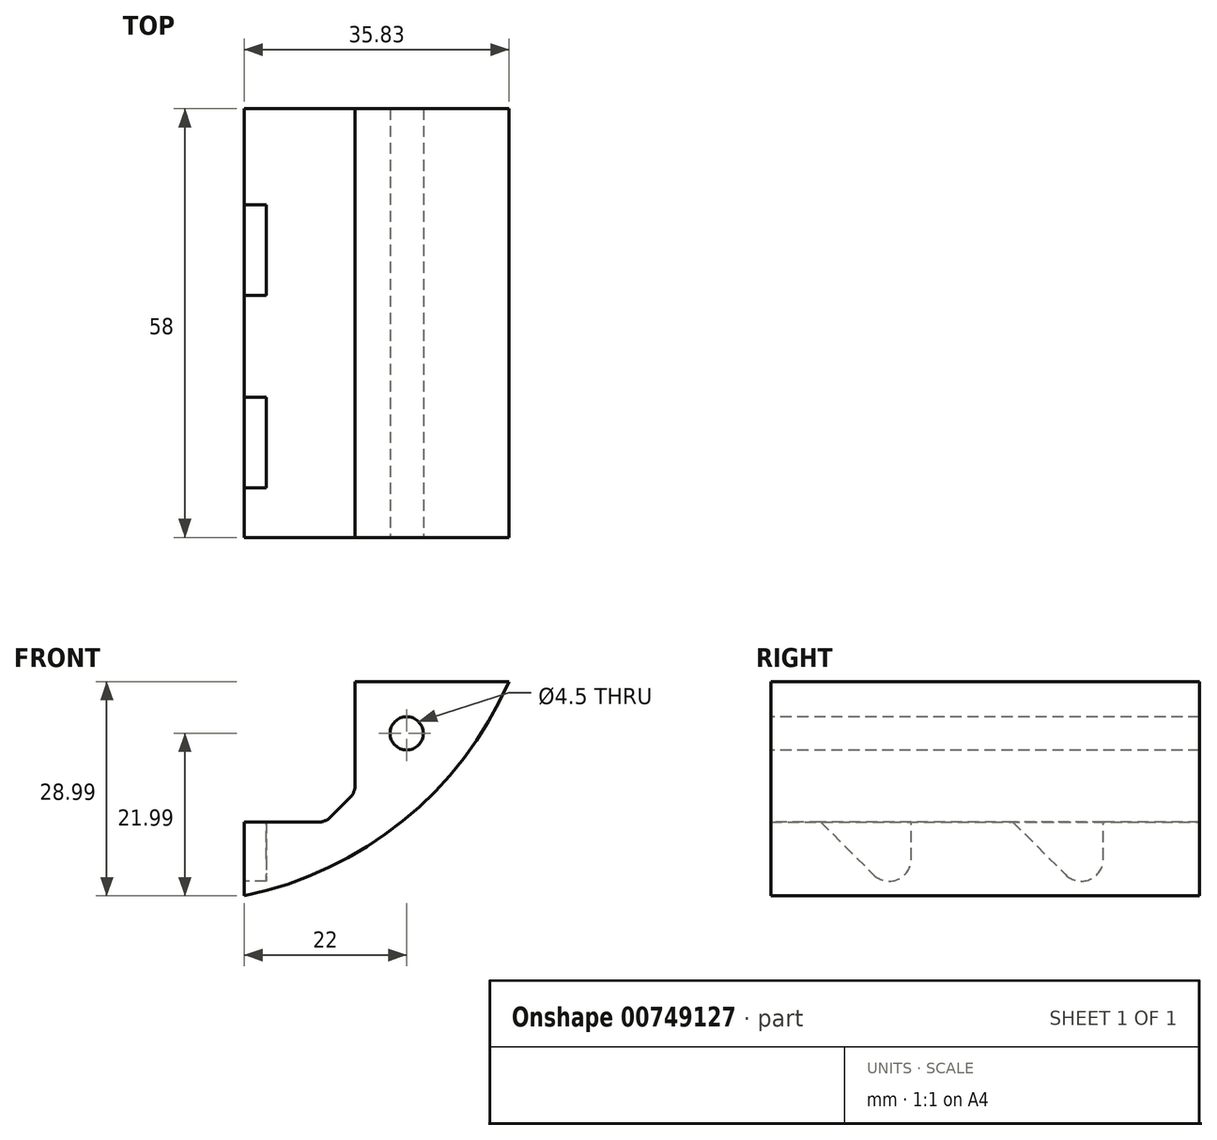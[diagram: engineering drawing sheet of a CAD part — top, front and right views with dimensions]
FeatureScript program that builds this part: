
annotation { "Feature Type Name" : "Feature", "Feature Type Description" : "" }
export const myFeature = defineFeature(function(context is Context, id is Id, definition is map)
    precondition{}
    {
        {
            var Q0;
            Q0=qCreatedBy(makeId("Front.planeOp"),FACE);
            var sketch = newSketch(context, id + "F0", { "sketchPlane" : qUnion([Q0])});
            skArc(sketch, "E0", {"start": v(10, -48.99) * mm, "mid": v(31.45, -38.87) * mm, "end": v(45.83, -20) * mm});
            skLineSegment(sketch, "E1", {"start": v(45.83, -20) * mm, "end": v(10, -20) * mm});
            skLineSegment(sketch, "E2", {"start": v(10, -20) * mm, "end": v(10, -48.99) * mm});
            skSolve(sketch);
        }
        {
            var Q0;
            Q0 = qSketchRegion(id + "F0", true);
            extrude(context, id + "F1", {"entities" : qUnion([Q0]), "endBound" : BoundingType.SYMMETRIC, "depth" : 58 * mm, "offsetDistance" : 25 * mm});
        }
        {
            var Q0;
            Q0=makeQuery(id+"F1.opExtrude","CAP_FACE",FACE,{"disambiguationData":[OSD([sQuery(id+"F0.wireOp",EDGE,"E0"),sQuery(id+"F0.wireOp",EDGE,"E1"),sQuery(id+"F0.wireOp",EDGE,"E2")])],"isStart":false});
            var sketch = newSketch(context, id + "F2", { "sketchPlane" : qUnion([Q0])});
            skLineSegment(sketch, "E3.bottom", {"start": v(10, -20) * mm, "end": v(25, -20) * mm});
            skLineSegment(sketch, "E3.top", {"start": v(10, -38.99) * mm, "end": v(25, -38.99) * mm});
            skLineSegment(sketch, "E3.left", {"start": v(10, -20) * mm, "end": v(10, -38.99) * mm});
            skLineSegment(sketch, "E3.right", {"start": v(25, -20) * mm, "end": v(25, -38.99) * mm});
            skSolve(sketch);
        }
        {
            var Q0;
            Q0 = qSketchRegion(id + "F2", true);
            extrude(context, id + "F3", {"entities" : qUnion([Q0]), "operationType" : NewBodyOperationType.REMOVE, "endBound" : BoundingType.THROUGH_ALL, "oppositeDirection" : true, "depth" : 25 * mm, "offsetDistance" : 25 * mm});
        }
        {
            var Q0;
            Q0=makeQuery(id+"F3.boolean.opBoolean","COPY",EDGE,{"derivedFrom":makeQuery(id+"F3.opExtrude","SWEPT_EDGE",EDGE,{"disambiguationData":[OSD([sQuery(id+"F2.wireOp",EDGE,"E3.top"),sQuery(id+"F2.wireOp",EDGE,"E3.right")])]})});
            chamfer(context, id + "F4", {"entities" : qUnion([Q0]), "width" : 4 * mm, "tangentPropagation" : true});
        }
        {
            var Q0;
            Q0=makeQuery(id+"F1.opExtrude","SWEPT_FACE",FACE,{"disambiguationData":[OSD([sQuery(id+"F0.wireOp",EDGE,"E2")])]});
            var sketch = newSketch(context, id + "F5", { "sketchPlane" : qUnion([Q0])});
            skLineSegment(sketch, "E4", {"start": v(0, -48.99) * mm, "end": v(0, -38.99) * mm, "construction": true});
            skLineSegment(sketch, "E5", {"start": v(0, -38.99) * mm, "end": v(-13, -38.99) * mm, "construction": true});
            skLineSegment(sketch, "E6", {"start": v(-13, -38.99) * mm, "end": v(-13, -48.99) * mm, "construction": true});
            skLineSegment(sketch, "E7", {"start": v(-13, -48.99) * mm, "end": v(0, -48.99) * mm, "construction": true});
            skArc(sketch, "E8", {"start": v(-16, -44) * mm, "mid": v(-14.15, -46.77) * mm, "end": v(-10.88, -46.12) * mm});
            skLineSegment(sketch, "E9", {"start": v(-13, -44) * mm, "end": v(-16, -44) * mm, "construction": true});
            skLineSegment(sketch, "E10", {"start": v(-16, -44) * mm, "end": v(-16, -38.99) * mm});
            skLineSegment(sketch, "E11", {"start": v(-16, -38.99) * mm, "end": v(-3.75, -38.99) * mm});
            skLineSegment(sketch, "E12", {"start": v(-3.75, -38.99) * mm, "end": v(-10.88, -46.12) * mm});
            skLineSegment(sketch, "E13", {"start": v(0, -38.99) * mm, "end": v(13, -38.99) * mm, "construction": true});
            skLineSegment(sketch, "E14", {"start": v(13, -38.99) * mm, "end": v(13, -48.99) * mm, "construction": true});
            skLineSegment(sketch, "E15", {"start": v(13, -48.99) * mm, "end": v(0, -48.99) * mm, "construction": true});
            skArc(sketch, "E16", {"start": v(10, -44) * mm, "mid": v(11.85, -46.77) * mm, "end": v(15.12, -46.12) * mm});
            skLineSegment(sketch, "E17", {"start": v(13, -44) * mm, "end": v(10, -44) * mm, "construction": true});
            skLineSegment(sketch, "E18", {"start": v(10, -44) * mm, "end": v(10, -38.99) * mm});
            skLineSegment(sketch, "E19", {"start": v(10, -38.99) * mm, "end": v(22.25, -38.99) * mm});
            skLineSegment(sketch, "E20", {"start": v(22.25, -38.99) * mm, "end": v(15.12, -46.12) * mm});
            skSolve(sketch);
        }
        {
            var Q0;
            Q0 = qSketchRegion(id + "F5", true);
            extrude(context, id + "F6", {"entities" : qUnion([Q0]), "operationType" : NewBodyOperationType.REMOVE, "oppositeDirection" : true, "depth" : 3 * mm, "offsetDistance" : 25 * mm});
        }
        {
            var Q0;
            Q0=makeQuery(id+"F1.opExtrude","CAP_FACE",FACE,{"disambiguationData":[OSD([sQuery(id+"F0.wireOp",EDGE,"E0"),sQuery(id+"F0.wireOp",EDGE,"E1"),sQuery(id+"F0.wireOp",EDGE,"E2")])],"isStart":false});
            var sketch = newSketch(context, id + "F7", { "sketchPlane" : qUnion([Q0])});
            skCircle(sketch, "E21", {"center": v(32, -27) * mm, "radius": 2.25 * mm});
            skSolve(sketch);
        }
        {
            var Q0;
            Q0 = qSketchRegion(id + "F7", true);
            extrude(context, id + "F8", {"entities" : qUnion([Q0]), "operationType" : NewBodyOperationType.REMOVE, "endBound" : BoundingType.THROUGH_ALL, "oppositeDirection" : true, "depth" : 25 * mm, "offsetDistance" : 25 * mm});
        }
        {
            var Q0;
            Q0=makeQuery(id+"F3.boolean.opBoolean","COPY",EDGE,{"derivedFrom":makeQuery(id+"F3.opExtrude","SWEPT_EDGE",EDGE,{"disambiguationData":[OSD([sQuery(id+"F0.wireOp",EDGE,"E1"),sQuery(id+"F2.wireOp",EDGE,"E3.bottom"),sQuery(id+"F2.wireOp",EDGE,"E3.right")])]})});
            var Q1;
            {var subQ0=sQuery(id+"F2.wireOp",EDGE,"E3.right");Q1=makeQuery(id+"F4.opChamfer","BLEND_EDGE",EDGE,{"blendedFrom":[makeQuery(id+"F3.boolean.opBoolean","COPY",EDGE,{"derivedFrom":makeQuery(id+"F3.opExtrude","SWEPT_EDGE",EDGE,{"disambiguationData":[OSD([sQuery(id+"F2.wireOp",EDGE,"E3.top"),subQ0])]})}),makeQuery(id+"F3.boolean.opBoolean","COPY",FACE,{"derivedFrom":makeQuery(id+"F3.opExtrude","SWEPT_FACE",FACE,{"disambiguationData":[OSD([subQ0])]})})],"blendedInto":[makeQuery(id+"F3.boolean.opBoolean","COPY",FACE,{"derivedFrom":makeQuery(id+"F3.opExtrude","SWEPT_FACE",FACE,{"disambiguationData":[OSD([subQ0])]})})]});}
            var Q2;
            {var subQ0=sQuery(id+"F2.wireOp",EDGE,"E3.top");Q2=makeQuery(id+"F4.opChamfer","BLEND_EDGE",EDGE,{"blendedFrom":[makeQuery(id+"F3.boolean.opBoolean","COPY",EDGE,{"derivedFrom":makeQuery(id+"F3.opExtrude","SWEPT_EDGE",EDGE,{"disambiguationData":[OSD([subQ0,sQuery(id+"F2.wireOp",EDGE,"E3.right")])]})}),makeQuery(id+"F3.boolean.opBoolean","COPY",FACE,{"derivedFrom":makeQuery(id+"F3.opExtrude","SWEPT_FACE",FACE,{"disambiguationData":[OSD([subQ0])]})})],"blendedInto":[makeQuery(id+"F3.boolean.opBoolean","COPY",FACE,{"derivedFrom":makeQuery(id+"F3.opExtrude","SWEPT_FACE",FACE,{"disambiguationData":[OSD([subQ0])]})})]});}
            fillet(context, id + "F9", {"entities" : qUnion([Q0, Q1, Q2]), "radius" : 2 * mm, "tangentPropagation" : true, "allowEdgeOverflow" : false});
        }
    });
